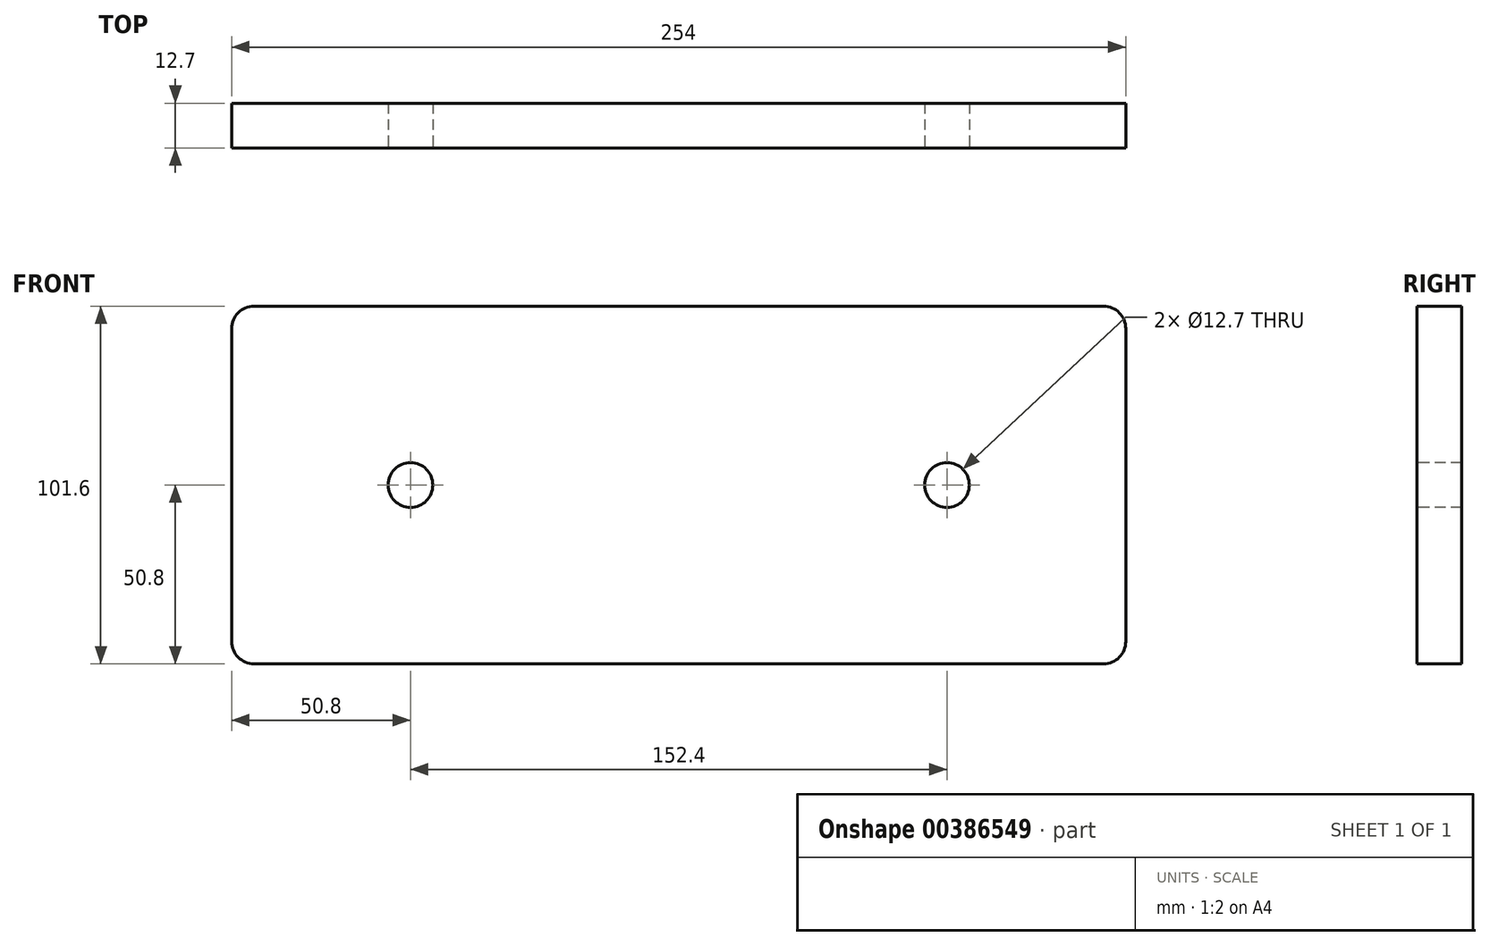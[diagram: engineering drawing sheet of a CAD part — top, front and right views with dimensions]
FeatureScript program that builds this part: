
annotation { "Feature Type Name" : "Feature", "Feature Type Description" : "" }
export const myFeature = defineFeature(function(context is Context, id is Id, definition is map)
    precondition{}
    {
        {
            var Q0;
            Q0=qCreatedBy(makeId("Front.planeOp"),FACE);
            var sketch = newSketch(context, id + "F0", { "sketchPlane" : qUnion([Q0])});
            skLineSegment(sketch, "E0.bottom", {"start": v(0, 0) * mm, "end": v(254, 0) * mm});
            skLineSegment(sketch, "E0.top", {"start": v(0, 101.6) * mm, "end": v(254, 101.6) * mm});
            skLineSegment(sketch, "E0.left", {"start": v(0, 0) * mm, "end": v(0, 101.6) * mm});
            skLineSegment(sketch, "E0.right", {"start": v(254, 0) * mm, "end": v(254, 101.6) * mm});
            skSolve(sketch);
        }
        {
            var Q0;
            Q0 = qSketchRegion(id + "F0", true);
            extrude(context, id + "F1", {"entities" : qUnion([Q0]), "depth" : 12.7 * mm});
        }
        {
            var Q0;
            Q0=makeQuery(id+"F1.opExtrude","CAP_FACE",FACE,{"disambiguationData":[OSD([sQuery(id+"F0.wireOp",EDGE,"E0.bottom"),sQuery(id+"F0.wireOp",EDGE,"E0.top"),sQuery(id+"F0.wireOp",EDGE,"E0.left"),sQuery(id+"F0.wireOp",EDGE,"E0.right")])],"isStart":false});
            var sketch = newSketch(context, id + "F2", { "sketchPlane" : qUnion([Q0])});
            skPoint(sketch, "E1", {"position": v(50.8, 50.8) * mm});
            skPoint(sketch, "E2", {"position": v(203.2, 50.8) * mm});
            skSolve(sketch);
        }
        {
            var Q0;
            Q0=sQuery(id+"F2.wireOp",VERTEX,"E1");
            var Q1;
            Q1=sQuery(id+"F2.wireOp",VERTEX,"E2");
            var Q2;
            Q2=makeQuery(id+"F1.opExtrude","SWEPT_BODY",BODY,{"disambiguationData":[OSD([sQuery(id+"F0.wireOp",EDGE,"E0.bottom"),sQuery(id+"F0.wireOp",EDGE,"E0.top"),sQuery(id+"F0.wireOp",EDGE,"E0.left"),sQuery(id+"F0.wireOp",EDGE,"E0.right")])]});
            hole(context, id + "F3", {"style" : HoleStyle.SIMPLE, "endStyle" : HoleEndStyle.THROUGH, "holeDiameter" : 12.7 * mm, "isTappedThrough" : true, "tappedDepth" : 12.7 * mm, "tapClearance" : 3, "locations" : qUnion([Q0, Q1]), "scope" : qUnion([Q2])});
        }
        {
            var Q0;
            Q0=makeQuery(id+"F1.opExtrude","SWEPT_EDGE",EDGE,{"disambiguationData":[OSD([sQuery(id+"F0.wireOp",EDGE,"E0.top"),sQuery(id+"F0.wireOp",EDGE,"E0.left")])]});
            var Q1;
            Q1=makeQuery(id+"F1.opExtrude","SWEPT_EDGE",EDGE,{"disambiguationData":[OSD([sQuery(id+"F0.wireOp",EDGE,"E0.bottom"),sQuery(id+"F0.wireOp",EDGE,"E0.left")])]});
            var Q2;
            Q2=makeQuery(id+"F1.opExtrude","SWEPT_EDGE",EDGE,{"disambiguationData":[OSD([sQuery(id+"F0.wireOp",EDGE,"E0.bottom"),sQuery(id+"F0.wireOp",EDGE,"E0.right")])]});
            var Q3;
            Q3=makeQuery(id+"F1.opExtrude","SWEPT_EDGE",EDGE,{"disambiguationData":[OSD([sQuery(id+"F0.wireOp",EDGE,"E0.top"),sQuery(id+"F0.wireOp",EDGE,"E0.right")])]});
            fillet(context, id + "F4", {"entities" : qUnion([Q0, Q1, Q2, Q3]), "radius" : 6.35 * mm, "tangentPropagation" : true, "allowEdgeOverflow" : false});
        }
    });
